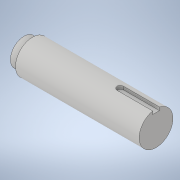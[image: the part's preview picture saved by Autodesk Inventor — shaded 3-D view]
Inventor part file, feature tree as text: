
AUTODESK INVENTOR PART (.ipt)
format: ipt  version: 2021 (Build 250183000, 183)  size: 124,416 bytes
history: native  units: in
note: dims shown in document units (in); Inventor stores cm internally (conversion verified against a paired STEP export)
features: extrude x4, sketch x4, plane x1
ambient origin geometry x8: Origin, YZ Plane, XZ Plane, XY Plane, X Axis, Y Axis, Z Axis, Center Point
bodies: Solid1 (feature_tree)
feature tree (9):
  extrude  "Extrusion1"  Depth=4.88in TaperAngle=0.0deg
  plane  "Work Plane1"
  extrude  "Extrusion9"  Depth=0.25in
  extrude  "Extrusion10"  Depth=0.125in TaperAngle=0.0deg
  extrude  "Extrusion11"  Depth=0.3125in TaperAngle=0.0deg
  sketch  "Sketch1"  dims[d0=1.25in d1=4.88in d2=0.0in]
  sketch  "Sketch9"  dims[d11=-2.0535in d26=0.25in]
  sketch  "Sketch10"  dims[d27=0.125in d28=1.313in d29=0.0in]
  sketch  "Sketch11"  dims[d30=1.0in d31=0.3125in d32=0.0in d33=1.0in d34=0.0in]
